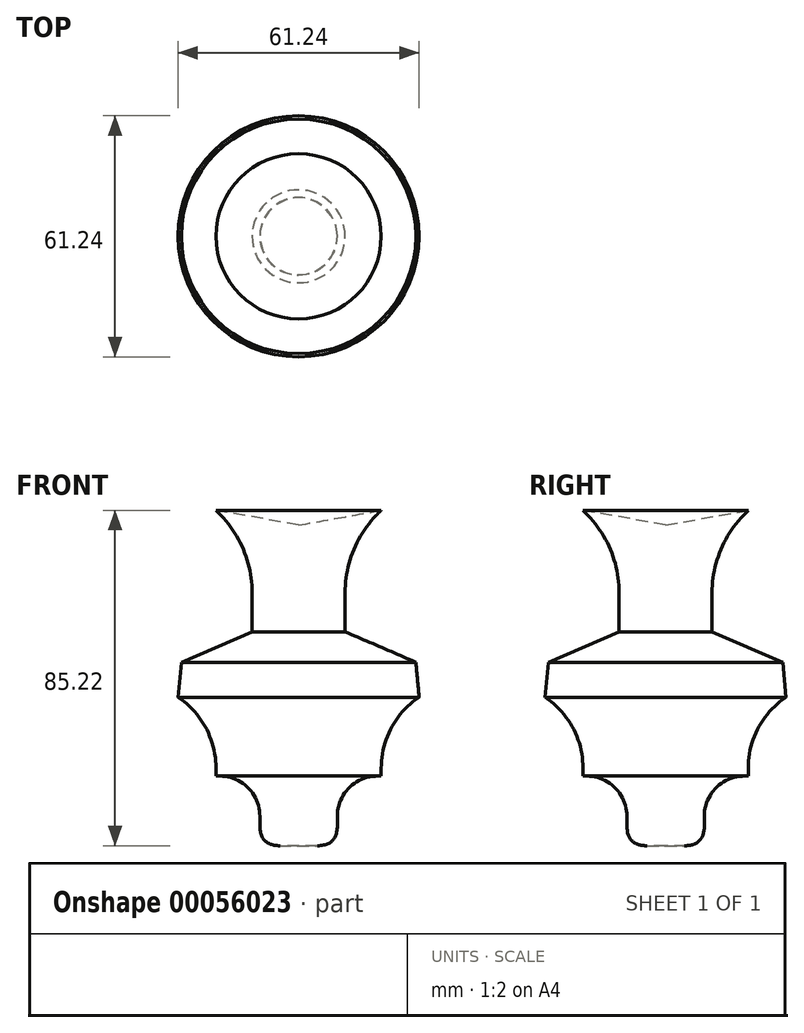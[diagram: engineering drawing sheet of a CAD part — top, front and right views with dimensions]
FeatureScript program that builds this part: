
annotation { "Feature Type Name" : "Feature", "Feature Type Description" : "" }
export const myFeature = defineFeature(function(context is Context, id is Id, definition is map)
    precondition{}
    {
        {
            var Q0;
            Q0=qCreatedBy(makeId("Front.planeOp"),FACE);
            var sketch = newSketch(context, id + "F0", { "sketchPlane" : qUnion([Q0])});
            skLineSegment(sketch, "E0", {"start": v(0, 38.52) * mm, "end": v(0, -42.93) * mm});
            skLineSegment(sketch, "E1", {"start": v(0, -42.93) * mm, "end": v(9.84, -42.93) * mm});
            skLineSegment(sketch, "E2", {"start": v(9.84, -42.93) * mm, "end": v(9.84, -35.46) * mm});
            skLineSegment(sketch, "E3", {"start": v(20.06, -25.24) * mm, "end": v(20.98, -25.24) * mm});
            skLineSegment(sketch, "E4", {"start": v(20.98, -25.24) * mm, "end": v(20.98, -23.23) * mm});
            skLineSegment(sketch, "E5", {"start": v(30.59, -5.22) * mm, "end": v(38.36, 0) * mm});
            skLineSegment(sketch, "E6", {"start": v(38.36, 0) * mm, "end": v(11.8, 11.44) * mm});
            skLineSegment(sketch, "E7", {"start": v(11.8, 11.44) * mm, "end": v(11.8, 21.34) * mm});
            skLineSegment(sketch, "E8", {"start": v(19.72, 40.97) * mm, "end": v(20.98, 42.29) * mm});
            skLineSegment(sketch, "E9", {"start": v(20.98, 42.29) * mm, "end": v(0, 38.52) * mm});
            skLineSegment(sketch, "E10", {"start": v(10.5, 40.4) * mm, "end": v(0, 38.52) * mm});
            skPoint(sketch, "E11.visualSharp", {"position": v(20.98, -11.67) * mm});
            skArc(sketch, "E11.filletArc", {"start": v(30.59, -5.22) * mm, "mid": v(23.53, -13.03) * mm, "end": v(20.98, -23.23) * mm});
            skPoint(sketch, "E12.visualSharp", {"position": v(9.84, -25.24) * mm});
            skArc(sketch, "E12.filletArc", {"start": v(20.06, -25.24) * mm, "mid": v(12.83, -28.23) * mm, "end": v(9.84, -35.46) * mm});
            skPoint(sketch, "E13.visualSharp", {"position": v(11.8, 32.75) * mm});
            skArc(sketch, "E13.filletArc", {"start": v(19.72, 40.97) * mm, "mid": v(13.86, 31.92) * mm, "end": v(11.8, 21.34) * mm});
            skSolve(sketch);
        }
        {
            var Q0;
            Q0=makeQuery(id+"F0.imprint","IMPRINT",FACE,{"disambiguationData":[TD([[makeQuery(id+"F0.imprint","IMPRINT",EDGE,{"derivedFrom":sQuery(id+"F0.wireOp",EDGE,"E0")}),1.0]])]});
            var Q1;
            Q1=sQuery(id+"F0.wireOp",EDGE,"E0");
            var Q2;
            Q2=sQuery(id+"F0.wireOp",EDGE,"E0");
            revolve(context, id + "F1", {"entities" : qUnion([Q0]), "surfaceEntities" : qUnion([Q1]), "axis" : qUnion([Q2]), "revolveType" : RevolveType.FULL});
        }
        {
            var Q0;
            Q0=makeQuery(id+"F1.opRevolve","SWEPT_EDGE",EDGE,{"disambiguationData":[OSD([sQuery(id+"F0.wireOp",EDGE,"E5"),sQuery(id+"F0.wireOp",EDGE,"E6")])]});
            chamfer(context, id + "F2", {"entities" : qUnion([Q0]), "width" : 5.08 * mm, "tangentPropagation" : true});
        }
        {
            var Q0;
            Q0=makeQuery(id+"F1.opRevolve","SWEPT_EDGE",EDGE,{"disambiguationData":[OSD([sQuery(id+"F0.wireOp",EDGE,"E1"),sQuery(id+"F0.wireOp",EDGE,"E2")])]});
            fillet(context, id + "F3", {"entities" : qUnion([Q0]), "radius" : 5.08 * mm, "tangentPropagation" : true, "rho" : 0.5, "crossSection" : FilletCrossSection.CONIC, "allowEdgeOverflow" : false});
        }
    });
